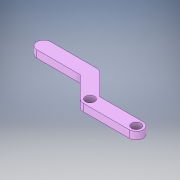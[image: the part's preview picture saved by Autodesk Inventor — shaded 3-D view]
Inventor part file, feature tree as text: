
AUTODESK INVENTOR PART (.ipt)
format: ipt  version: 2019 (Build 230136000, 136)  size: 134,656 bytes
history: native  units: mm
features: other x1, extrude x1, sketch x1
ambient origin geometry x8: Origin, YZ Plane, XZ Plane, XY Plane, X Axis, Y Axis, Z Axis, Center Point
bodies: Body1 (feature_tree)
feature tree (3):
  other  "Sólido1"
  extrude  "Extrusión1"  Depth=6.0mm
  sketch  "Boceto1"  dims[d0=4.0mm d1=6.0mm d2=20.0mm d3=4.0mm d4=6.0mm d5=5.0mm d6=5.0mm d7=6.0mm d8=20.0mm d9=3.18mm d10=0.0mm]
